# Revit family: Window-Casement-Pella-Architect_Series-Quarter_Circle
name_source: partatom
category: Windows
revit_build: Autodesk Revit Architecture 2013 (Build: 20130531_2115(x64)
units: mm (PartAtom-declared; Revit-internal decimal feet)

## types (8) — shared parameters
Analytic Construction = <None>
Architectural Data Sheet = To be determined
Architectural Design Manual = www.pellaadm.com
Construction Type = -
Custom Arc Radius = No
Custom Grille Pattern = Yes
Default Sill Height = 2' - 7 1/2"
Description = Casement Quarter Circle
Egress Window = No
Energy Efficiency = http://www.pella.com
Environmental Commitment = http://www.pella.com
Ext Finish = Aluminum - Pella - Brown
Glazing Finish = Glass - Pella - Clear Insulating Glass
Glazing Thickness = 0' - 0 5/8"
Grille Note = To adjust Number of Arcs see Custom Arc Number in Type Parameters
Grille Visibility = Yes
Heat Transfer Coefficient (U) = 0.1000 BTU/(h·ft²·°F)
Int Finish = Wood - Pella - Pine
Manufacturer = Pella Windows & Doors
Number of Arcs = 4
Operation = Fixed
Product Documentation Link = http://media.pella.com
Product Name = Architect Series Quarter Circle
Product Page URL = http://www.pella.com
Series = Architect Series - Aluminum-Clad Wood
Size Constraints = Window Sizing constraints available in 6.35 mm increments
Thermal Resistance (R) = 10.0000 (h·ft²·°F)/BTU
URL = www.pella.com
Wall Closure = By host
zero-valued in all types: Solar Heat Gain Coefficient, Visual Light Transmittance

## per-type parameters (varying)
| type | C Radius | Head Height | Height | Rough Height | Rough Width | Sash Height | Sash Width | Unit Height | Unit Width | Width |
| 2121 | 1' - 9" | 4' - 4 1/2" | 1' - 9" | 1' - 9 3/4" | 1' - 9 3/4" | 1' - 6 1/2" | 1' - 6 1/2" | 1' - 9" | 1' - 9" | 1' - 9" |
| 2525 | 2' - 1" | 4' - 8 1/2" | 2' - 1" | 2' - 1 3/4" | 2' - 1 3/4" | 1' - 10 1/2" | 1' - 10 1/2" | 2' - 1" | 2' - 1" | 2' - 1" |
| 2929 | 2' - 5" | 5' - 0 1/2" | 2' - 5" | 2' - 5 3/4" | 2' - 5 3/4" | 2' - 2 1/2" | 2' - 2 1/2" | 2' - 5" | 2' - 5" | 2' - 5" |
| 3333 | 2' - 9" | 5' - 4 1/2" | 2' - 9" | 2' - 9 3/4" | 2' - 9 3/4" | 2' - 6 1/2" | 2' - 6 1/2" | 2' - 9" | 2' - 9" | 2' - 9" |
| 3535 | 2' - 11" | 5' - 6 1/2" | 2' - 11" | 2' - 11 3/4" | 2' - 11 3/4" | 2' - 8 1/2" | 2' - 8 1/2" | 2' - 11" | 2' - 11" | 2' - 11" |
| 3737 | 3' - 1" | 5' - 8 1/2" | 3' - 1" | 3' - 1 3/4" | 3' - 1 3/4" | 2' - 10 1/2" | 2' - 10 1/2" | 3' - 1" | 3' - 1" | 3' - 1" |
| 4141 | 3' - 5" | 6' - 0 1/2" | 3' - 5" | 3' - 5 3/4" | 3' - 5 3/4" | 3' - 2 1/2" | 3' - 2 1/2" | 3' - 5" | 3' - 5" | 3' - 5" |
| 4545 | 3' - 9" | 6' - 4 1/2" | 3' - 9" | 3' - 9 3/4" | 3' - 9 3/4" | 3' - 6 1/2" | 3' - 6 1/2" | 3' - 9" | 3' - 9" | 3' - 9" |

note: column(s) folded — value = type name in every type: Model

## geometry (parser evidence)
native form markers: Blend x10, Sweep x3
no freeform markers — native parametric forms only
